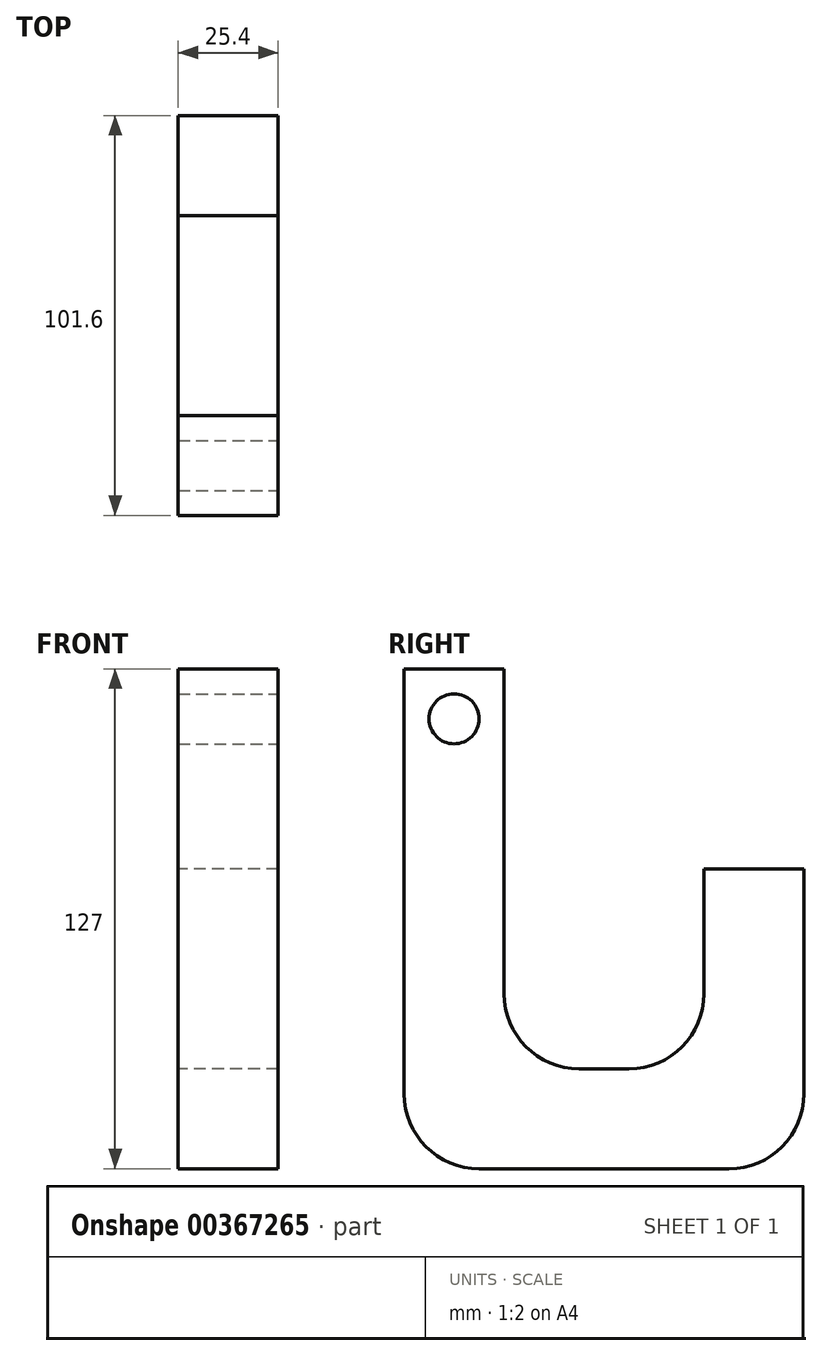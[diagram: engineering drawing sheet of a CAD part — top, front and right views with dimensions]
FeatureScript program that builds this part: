
annotation { "Feature Type Name" : "Feature", "Feature Type Description" : "" }
export const myFeature = defineFeature(function(context is Context, id is Id, definition is map)
    precondition{}
    {
        {
            var Q0;
            Q0=qCreatedBy(makeId("Front.planeOp"),FACE);
            var sketch = newSketch(context, id + "F0", { "sketchPlane" : qUnion([Q0])});
            skPoint(sketch, "E0", {"position": v(-25.4, 25.4) * mm});
            skLineSegment(sketch, "E1.bottom", {"start": v(0, 0) * mm, "end": v(-25.4, 0) * mm});
            skLineSegment(sketch, "E1.top", {"start": v(0, 25.4) * mm, "end": v(-25.4, 25.4) * mm});
            skLineSegment(sketch, "E1.left", {"start": v(0, 0) * mm, "end": v(0, 25.4) * mm});
            skLineSegment(sketch, "E1.right", {"start": v(-25.4, 0) * mm, "end": v(-25.4, 25.4) * mm});
            skSolve(sketch);
        }
        {
            var Q0;
            Q0 = qSketchRegion(id + "F0", true);
            extrude(context, id + "F1", {"entities" : qUnion([Q0]), "depth" : 101.6 * mm});
        }
        {
            var Q0;
            Q0=makeQuery(id+"F1.opExtrude","SWEPT_FACE",FACE,{"disambiguationData":[OSD([sQuery(id+"F0.wireOp",EDGE,"E1.bottom")])]});
            var sketch = newSketch(context, id + "F2", { "sketchPlane" : qUnion([Q0])});
            skPoint(sketch, "E2", {"position": v(0, 76.2) * mm});
            skLineSegment(sketch, "E3.bottom", {"start": v(-25.4, 101.6) * mm, "end": v(0, 101.6) * mm});
            skLineSegment(sketch, "E3.top", {"start": v(-25.4, 76.2) * mm, "end": v(0, 76.2) * mm});
            skLineSegment(sketch, "E3.left", {"start": v(-25.4, 101.6) * mm, "end": v(-25.4, 76.2) * mm});
            skLineSegment(sketch, "E3.right", {"start": v(0, 101.6) * mm, "end": v(0, 76.2) * mm});
            skSolve(sketch);
        }
        {
            var Q0;
            Q0 = qSketchRegion(id + "F2", true);
            extrude(context, id + "F3", {"entities" : qUnion([Q0]), "operationType" : NewBodyOperationType.ADD, "depth" : -127 * mm});
        }
        {
            var Q0;
            Q0=makeQuery(id+"F1.opExtrude","SWEPT_FACE",FACE,{"disambiguationData":[OSD([sQuery(id+"F0.wireOp",EDGE,"E1.bottom")])]});
            var sketch = newSketch(context, id + "F4", { "sketchPlane" : qUnion([Q0])});
            skPoint(sketch, "E4", {"position": v(-25.4, 25.4) * mm});
            skLineSegment(sketch, "E5.bottom", {"start": v(0, 0) * mm, "end": v(-25.4, 0) * mm});
            skLineSegment(sketch, "E5.top", {"start": v(0, 25.4) * mm, "end": v(-25.4, 25.4) * mm});
            skLineSegment(sketch, "E5.left", {"start": v(0, 0) * mm, "end": v(0, 25.4) * mm});
            skLineSegment(sketch, "E5.right", {"start": v(-25.4, 0) * mm, "end": v(-25.4, 25.4) * mm});
            skSolve(sketch);
        }
        {
            var Q0;
            Q0=makeQuery(id+"F4.imprint","IMPRINT",FACE,{"disambiguationData":[TD([[makeQuery(id+"F4.imprint","IMPRINT",EDGE,{"derivedFrom":sQuery(id+"F4.wireOp",EDGE,"E5.bottom")}),-1.0]])]});
            extrude(context, id + "F5", {"entities" : qUnion([Q0]), "operationType" : NewBodyOperationType.ADD, "depth" : -76.2 * mm});
        }
        {
            var Q0;
            Q0=makeQuery(id+"F5.boolean.opBoolean","MERGE",FACE,{"derivedFrom":[makeQuery(id+"F3.boolean.opBoolean","MERGE",FACE,{"derivedFrom":[makeQuery(id+"F1.opExtrude","SWEPT_FACE",FACE,{"disambiguationData":[OSD([sQuery(id+"F0.wireOp",EDGE,"E1.left")])]}),makeQuery(id+"F3.opExtrude","SWEPT_FACE",FACE,{"disambiguationData":[OSD([sQuery(id+"F2.wireOp",EDGE,"E3.right")])]})]}),makeQuery(id+"F5.opExtrude","SWEPT_FACE",FACE,{"disambiguationData":[OSD([sQuery(id+"F4.wireOp",EDGE,"E5.left")])]})]});
            var sketch = newSketch(context, id + "F6", { "sketchPlane" : qUnion([Q0])});
            skCircle(sketch, "E6", {"center": v(-88.9, 114.3) * mm, "radius": 6.35 * mm});
            skLineSegment(sketch, "E7", {"start": v(-88.9, 127) * mm, "end": v(-88.9, 114.3) * mm});
            skLineSegment(sketch, "E8", {"start": v(-88.9, 114.3) * mm, "end": v(-76.2, 114.3) * mm});
            skSolve(sketch);
        }
        {
            var Q0;
            Q0=sQuery(id+"F6.wireOp",VERTEX,"E6.center");
            var Q1;
            Q1=makeQuery(id+"F1.opExtrude","SWEPT_BODY",BODY,{"disambiguationData":[OSD([sQuery(id+"F0.wireOp",EDGE,"E1.bottom"),sQuery(id+"F0.wireOp",EDGE,"E1.top"),sQuery(id+"F0.wireOp",EDGE,"E1.left"),sQuery(id+"F0.wireOp",EDGE,"E1.right")])]});
            hole(context, id + "F7", {"style" : HoleStyle.SIMPLE, "endStyle" : HoleEndStyle.THROUGH, "holeDiameter" : 12.7 * mm, "isTappedThrough" : true, "tappedDepth" : 12.7 * mm, "tapClearance" : 3, "locations" : qUnion([Q0]), "scope" : qUnion([Q1])});
        }
        {
            var Q0;
            Q0=makeQuery(id+"F3.boolean.opBoolean","INTERSECT",EDGE,{"derivedFrom":[makeQuery(id+"F1.opExtrude","SWEPT_FACE",FACE,{"disambiguationData":[OSD([sQuery(id+"F0.wireOp",EDGE,"E1.top")])]}),makeQuery(id+"F3.opExtrude","SWEPT_FACE",FACE,{"disambiguationData":[OSD([sQuery(id+"F2.wireOp",EDGE,"E3.top")])]})]});
            fillet(context, id + "F8", {"entities" : qUnion([Q0]), "radius" : 19.05 * mm, "tangentPropagation" : true, "allowEdgeOverflow" : false});
        }
        {
            var Q0;
            Q0=makeQuery(id+"F1.opExtrude","CAP_EDGE",EDGE,{"disambiguationData":[OSD([sQuery(id+"F0.wireOp",EDGE,"E1.bottom")])],"isStart":false});
            fillet(context, id + "F9", {"entities" : qUnion([Q0]), "radius" : 19.05 * mm, "tangentPropagation" : true, "allowEdgeOverflow" : false});
        }
        {
            var Q0;
            Q0=makeQuery(id+"F1.opExtrude","CAP_EDGE",EDGE,{"disambiguationData":[OSD([sQuery(id+"F0.wireOp",EDGE,"E1.bottom")])],"isStart":true});
            fillet(context, id + "F10", {"entities" : qUnion([Q0]), "radius" : 19.05 * mm, "tangentPropagation" : true, "allowEdgeOverflow" : false});
        }
        {
            var Q0;
            Q0=makeQuery(id+"F5.boolean.opBoolean","INTERSECT",EDGE,{"derivedFrom":[makeQuery(id+"F1.opExtrude","SWEPT_FACE",FACE,{"disambiguationData":[OSD([sQuery(id+"F0.wireOp",EDGE,"E1.top")])]}),makeQuery(id+"F5.opExtrude","SWEPT_FACE",FACE,{"disambiguationData":[OSD([sQuery(id+"F4.wireOp",EDGE,"E5.top")])]})]});
            fillet(context, id + "F11", {"entities" : qUnion([Q0]), "radius" : 19.05 * mm, "tangentPropagation" : true, "allowEdgeOverflow" : false});
        }
    });
